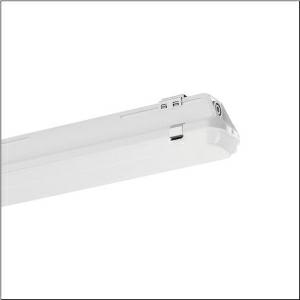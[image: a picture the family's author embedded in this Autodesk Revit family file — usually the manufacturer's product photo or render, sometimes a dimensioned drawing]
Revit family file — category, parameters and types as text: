
# Revit family: monsun_21_emergency_51fb10dl447k3h
name_source: partatom
category: Lighting Fixtures
units: mm (PartAtom-declared; Revit-internal decimal feet)

## family parameters
Cut with Voids When Loaded = No
Host = Face
Light Source = No
Part Type = Normal
Room Calculation Point = No
Round Connector Dimension = Use Diameter
Shared = No

## types (1)
- --- (1 x LED, 4330 lm, 28.1 W, 4000K)
    Apparent Load = 28 VA
    CIE Flux Codes = 46 76 93 94 100
    Color Rendering = 80
    Color Temperature = 4000K
    Default Elevation = 1800 mm
    Description = Monsun 21 emergency, damp-proof luminaire, chain hanger, primary optical cover: enclosure, of PMMA, light emission: direct distribution, primary light characteristic: symmetric, installation type: vertical mounting, horizontal mounting, surface-mounted, suspended mounting, LED, rated luminous flux: 4.330lm, luminous efficacy: 178lm/W, light colour: 840, colour temperature: 4000K, control gear: DALI 2, with terminal, 5-pole, max. 2.5mm², mains connection: 220..240V, AC, 50/60Hz, rated input power: 28W, control gear: single battery element, battery: LiFePO4, 9Ah, housing, of glass-fibre reinforced plastic, uncoated, bright grey, incl. chain hanger, length: 1.299mm, width: 90mm, height: 88mm, clip for enclosure, of stainless steel (V2A), ceiling mounting element, of stainless steel (V2A), chain hanger, of stainless steel (V2A), protection rating (complete): IP66, insulation class (complete): insulation class I (protective earthing), certification: CE, UKCA, protection symbol: D, impact resistance: IK04, permissible operating ambient temperature: +5..+25°C, standard: EN 50419, EN 60598-2-1, corresponds to IFS (International Featured Standards) requirements for safety and quality in the food industry, for indoor or canopied outdoor use, no direct snow, no direct sun, no direct rain, LABS conformity tested according to VDMA 24364:2018-05, contact your sales advisor before using the luminaires in applications with unclear chemical exposure, large temperature fluctuations or condensation-forming humidity, packaging unit: 1 piece
    Height = 88 mm
    Lamp = 1 x LED
    Lamp Light Flux = 4330 lm
    Lamp Power = 28.1 W
    Lamp count = 1
    Length = 1299 mm
    Luminous efficacy = 154 lm/W
    Manufacturer = Siteco
    ModVariant = No
    Model = 51FB10DL447K3H
    Mounting Place = Ceiling
    Mounting Type = Surface mounted
    Number of Poles = 1
    OnlyDefault = Yes
    Power Factor = 1
    Product Name = Monsun 21 emergency
    Product group = damp-proof luminaire
    ProductGroupID = 300
    Protection Class = Protection class I
    Protection Degree = IP 66
    RLX_Detail_Level = 1
    RLX_Emergency_Light_Flux = 0 lm
    RLX_Emergency_Type = 0
    RLX_Emergency_Type_DB = No
    RlxData = <blob elided: 93489 chars, md5=aad92a04>
    Socket = socket
    Standby Power = 0 W
    System Light Flux = 4330 lm
    System Power = 28 W
    Type Comments = : luminous flux: 100 % | dim-lin: 254 | 164 mA
    Type Image = l_1319656.jpg
    URL = http://relux.com
    VarID = @adj_037263
    Voltage = 0 V
    Weight = 0.00 kg
    Width = 90 mm

## geometry (parser evidence)
native form markers: Blend x4, Sweep x12
no freeform markers — native parametric forms only
